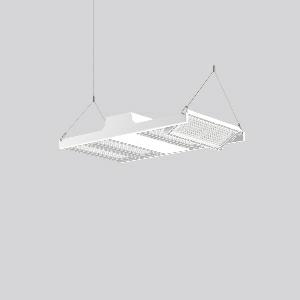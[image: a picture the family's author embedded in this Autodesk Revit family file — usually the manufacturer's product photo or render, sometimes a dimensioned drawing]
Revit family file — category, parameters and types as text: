
# Revit family: light_case_921686_002_76_7c8e
name_source: partatom
category: Lighting Fixtures
units: mm (PartAtom-declared; Revit-internal decimal feet)

## family parameters
Cut with Voids When Loaded = No
Host = Face
Light Source = No
Part Type = Normal
Room Calculation Point = No
Round Connector Dimension = Use Diameter
Shared = No

## types (1)
- LIGHT CASE (1 x LED Modul 840, 8825 lm, 4000)
    Apparent Load = 225 VA
    CIE Flux Codes = 89 96 99 100 100
    Color Rendering = 80
    Color Temperature = 4000
    Default Elevation = 1800 mm
    Description = Series: LIGHT CASE
Flat highbay luminaire for chain or cable suspension with 4 LED modules that can be swivelled. Housing: die cast aluminium and sheet steel, powder-coated. Optimised thermal management thanks to special luminaire design. Self-cleaning heat sink for constant heat dissipation. Cover: plastic (polycarbonate, shockproof), with integrated four-row lens system. LED modules can be swivelled ± 30° for optimum illumination. Suitable for chain or steel cable suspension (to be provided on site). With 5-pin connection terminal (1.5 m). With integrated movement sensor and light sensor for daylight detection on request. Ball impact proof in accordance with DIN 18032-03 (except steel cable suspension). Luminaire with limited surface temperature in accordance with EN 60598-2-24 for use in environments in which a deposit of conductive dust on the luminaire can be expected. 
Colour: white
Length: 680 mm
Width: 397 mm
Height: 110 mm
Lamp: LED
Socket: without socket
Colour temperature: 4000K
Colour rendering index (CRI): 80
System power: 225 W
Rated luminous flux: 35300 lm
Luminous efficiency: 157 lm/W
Control gear: Converter, dimmable, DALI
Protection class: I
Type of protection: IP 65
    Height = 110 mm
    Lamp = 1 x LED Modul 840
    Lamp Light Flux = 8825 lm
    Lamp count = 1
    Length = 680 mm
    Lifetime = 50000 h
    Luminous efficacy = 157 lm/W
    Manufacturer = RZB
    ModVariant = No
    Model = 921686.002.76
    Mounting Place = Ceiling
    Mounting Type = Pendant
    Number of Poles = 1
    OnlyDefault = Yes
    Power Factor = 1
    Product Name = LIGHT CASE
    Product group = Pendant commercial luminaires
    ProductGroupID = 903
    Protection Class = Protection class I
    Protection Degree = IP 65
    RLX_Detail_Level = 1
    RLX_Emergency_Light_Flux = 0 lm
    RLX_Emergency_Type = 0
    RLX_Emergency_Type_DB = No
    RlxData = <blob elided: 28445 chars, md5=4fba7883>
    Socket = socket
    Standby Power = 0 W
    System Light Flux = 35300 lm
    System Power = 225 W
    Type Comments = Product without accessories
    Type Image = 921523.002.76.jpg
    URL = http://relux.com
    VarID = ---
    Voltage = 230 V
    Voltage Range = 220-240 V
    Weight = 0.00 kg
    Width = 397 mm

## geometry (parser evidence)
native form markers: Blend x4, Sweep x19
no freeform markers — native parametric forms only
